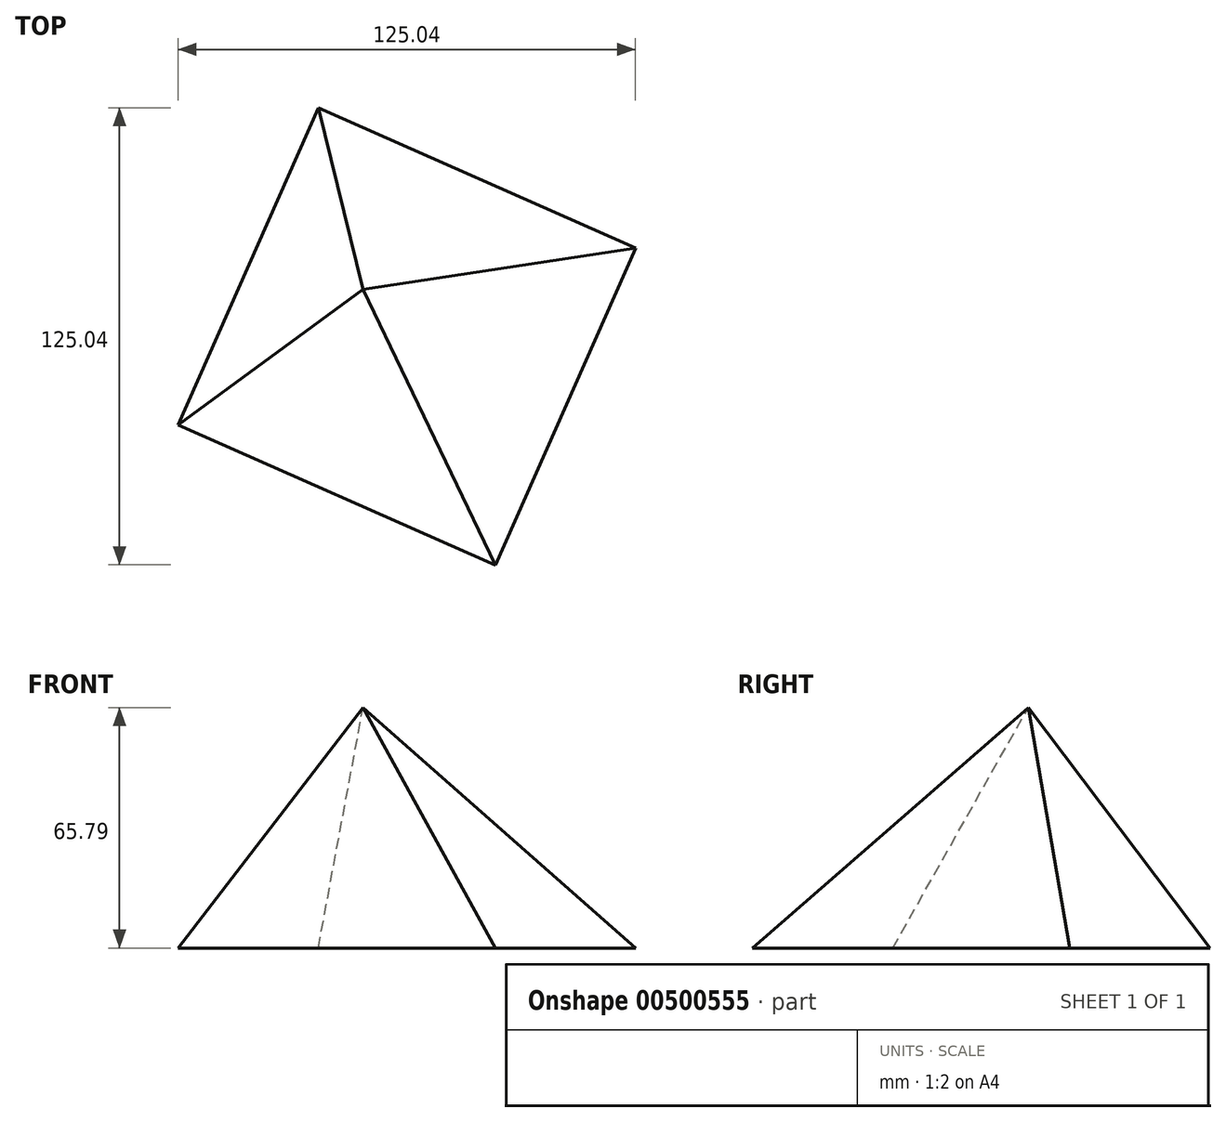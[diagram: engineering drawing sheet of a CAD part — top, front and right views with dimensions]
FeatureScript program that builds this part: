
annotation { "Feature Type Name" : "Feature", "Feature Type Description" : "" }
export const myFeature = defineFeature(function(context is Context, id is Id, definition is map)
    precondition{}
    {
        {
            var Q0;
            Q0=qCreatedBy(makeId("Top.planeOp"),FACE);
            var sketch = newSketch(context, id + "F0", { "sketchPlane" : qUnion([Q0])});
            skCircle(sketch, "E0.cCircle", {"center": v(0, 0) * mm, "radius": 67.04 * mm, "construction": true});
            skLineSegment(sketch, "E0.0", {"start": v(-24.2, 62.52) * mm, "end": v(62.52, 24.2) * mm});
            skLineSegment(sketch, "E0.1", {"start": v(62.52, 24.2) * mm, "end": v(24.2, -62.52) * mm});
            skLineSegment(sketch, "E0.2", {"start": v(24.2, -62.52) * mm, "end": v(-62.52, -24.2) * mm});
            skLineSegment(sketch, "E0.3", {"start": v(-62.52, -24.2) * mm, "end": v(-24.2, 62.52) * mm});
            skSolve(sketch);
        }
        {
            var Q0;
            Q0=qCreatedBy(makeId("Top.planeOp"),FACE);
            cPlane(context, id + "F1", {"entities" : qUnion([Q0]), "cplaneType" : CPlaneType.OFFSET, "offset" : 65.8 * mm, "width" : 152.4 * mm, "height" : 152.4 * mm});
        }
        {
            var Q0;
            Q0=qCreatedBy(id+"F1.planeOp",FACE);
            var sketch = newSketch(context, id + "F2", { "sketchPlane" : qUnion([Q0])});
            skPoint(sketch, "E1", {"position": v(-11.96, 12.84) * mm});
            skSolve(sketch);
        }
        {
            var Q0;
            Q0=makeQuery(id+"F0.imprint","IMPRINT",FACE,{"disambiguationData":[TD([[makeQuery(id+"F0.imprint","IMPRINT",EDGE,{"derivedFrom":sQuery(id+"F0.wireOp",EDGE,"E0.0")}),-1.0]])]});
            var Q1;
            Q1=sQuery(id+"F2.wireOp",VERTEX,"E1");
            loft(context, id + "F3", {"sheetProfilesArray" : [{ "sheetProfileEntities" : qUnion([Q0]) }, { "sheetProfileEntities" : qUnion([Q1]) }]});
        }
    });
